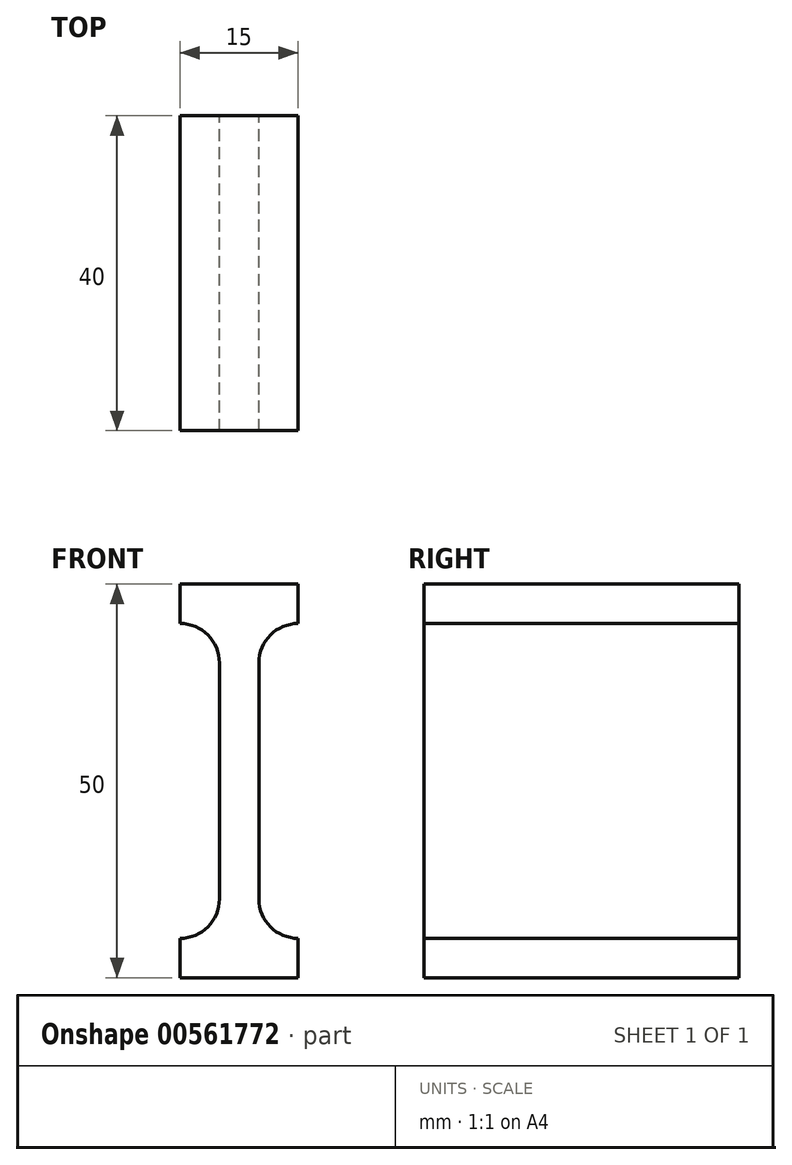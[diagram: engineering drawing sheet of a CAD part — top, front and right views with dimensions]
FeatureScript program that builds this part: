
annotation { "Feature Type Name" : "Feature", "Feature Type Description" : "" }
export const myFeature = defineFeature(function(context is Context, id is Id, definition is map)
    precondition{}
    {
        {
            var Q0;
            Q0=qCreatedBy(makeId("Front.planeOp"),FACE);
            var sketch = newSketch(context, id + "F0", { "sketchPlane" : qUnion([Q0])});
            skLineSegment(sketch, "E0", {"start": v(-25.26, 50) * mm, "end": v(-10.26, 50) * mm});
            skLineSegment(sketch, "E1", {"start": v(-10.26, 50) * mm, "end": v(-10.26, 45) * mm});
            skLineSegment(sketch, "E2", {"start": v(-10.26, 45) * mm, "end": v(-15.26, 45) * mm});
            skLineSegment(sketch, "E3", {"start": v(-15.26, 45) * mm, "end": v(-15.26, 5) * mm});
            skLineSegment(sketch, "E4", {"start": v(-15.26, 5) * mm, "end": v(-10.26, 5) * mm});
            skLineSegment(sketch, "E5", {"start": v(-10.26, 5) * mm, "end": v(-10.26, 0) * mm});
            skLineSegment(sketch, "E6", {"start": v(-10.26, 0) * mm, "end": v(-25.26, 0) * mm});
            skLineSegment(sketch, "E7", {"start": v(-25.26, 0) * mm, "end": v(-25.26, 5) * mm});
            skLineSegment(sketch, "E8", {"start": v(-25.26, 5) * mm, "end": v(-20.26, 5) * mm});
            skLineSegment(sketch, "E9", {"start": v(-20.26, 5) * mm, "end": v(-20.26, 45) * mm});
            skLineSegment(sketch, "E10", {"start": v(-20.26, 45) * mm, "end": v(-25.26, 45) * mm});
            skLineSegment(sketch, "E11", {"start": v(-25.26, 45) * mm, "end": v(-25.26, 50) * mm});
            skSolve(sketch);
        }
        {
            var Q0;
            Q0=makeQuery(id+"F0.imprint","IMPRINT",FACE,{"disambiguationData":[TD([[makeQuery(id+"F0.imprint","IMPRINT",EDGE,{"derivedFrom":sQuery(id+"F0.wireOp",EDGE,"E0")}),-1.0]])]});
            extrude(context, id + "F1", {"entities" : qUnion([Q0]), "depth" : 40 * mm, "offsetDistance" : 25 * mm});
        }
        {
            var Q0;
            Q0=makeQuery(id+"F1.opExtrude","SWEPT_EDGE",EDGE,{"disambiguationData":[OSD([sQuery(id+"F0.wireOp",EDGE,"E3"),sQuery(id+"F0.wireOp",EDGE,"E4")])]});
            var Q1;
            Q1=makeQuery(id+"F1.opExtrude","SWEPT_EDGE",EDGE,{"disambiguationData":[OSD([sQuery(id+"F0.wireOp",EDGE,"E8"),sQuery(id+"F0.wireOp",EDGE,"E9")])]});
            var Q2;
            Q2=makeQuery(id+"F1.opExtrude","SWEPT_EDGE",EDGE,{"disambiguationData":[OSD([sQuery(id+"F0.wireOp",EDGE,"E2"),sQuery(id+"F0.wireOp",EDGE,"E3")])]});
            var Q3;
            Q3=makeQuery(id+"F1.opExtrude","SWEPT_EDGE",EDGE,{"disambiguationData":[OSD([sQuery(id+"F0.wireOp",EDGE,"E9"),sQuery(id+"F0.wireOp",EDGE,"E10")])]});
            fillet(context, id + "F2", {"entities" : qUnion([Q0, Q1, Q2, Q3]), "radius" : 5 * mm, "tangentPropagation" : true, "allowEdgeOverflow" : false});
        }
    });
